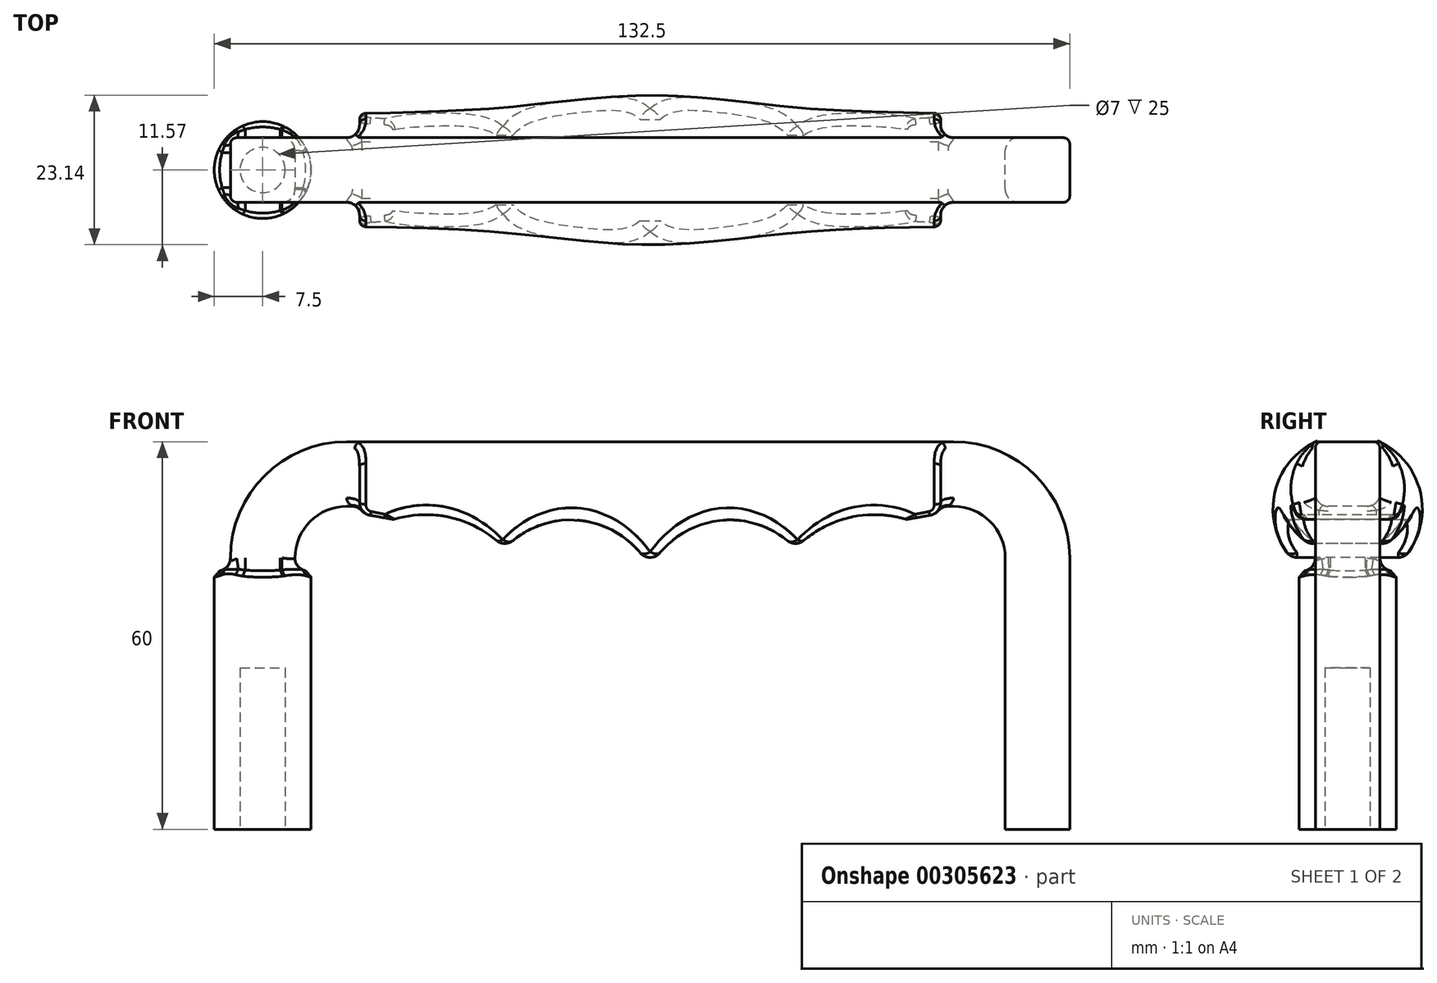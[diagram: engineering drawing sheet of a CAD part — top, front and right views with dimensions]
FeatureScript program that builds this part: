
annotation { "Feature Type Name" : "Feature", "Feature Type Description" : "" }
export const myFeature = defineFeature(function(context is Context, id is Id, definition is map)
    precondition{}
    {
        {
            var Q0;
            Q0=qCreatedBy(makeId("Front.planeOp"),FACE);
            var sketch = newSketch(context, id + "F0", { "sketchPlane" : qUnion([Q0])});
            skLineSegment(sketch, "E0", {"start": v(-60, 0) * mm, "end": v(-60, 55) * mm});
            skLineSegment(sketch, "E1", {"start": v(-60, 55) * mm, "end": v(60, 55) * mm});
            skLineSegment(sketch, "E2", {"start": v(60, 55) * mm, "end": v(60, 0) * mm});
            skPoint(sketch, "E3", {"position": v(0, 55) * mm});
            skSolve(sketch);
        }
        {
            var Q0;
            Q0=sQuery(id+"F0.wireOp",EDGE,"E0");
            var Q1;
            Q1=sQuery(id+"F0.wireOp",VERTEX,"E0.start");
            cPlane(context, id + "F1", {"entities" : qUnion([Q0, Q1]), "cplaneType" : CPlaneType.CURVE_POINT, "offset" : 25 * mm, "width" : 150 * mm, "height" : 150 * mm});
        }
        {
            var Q0;
            Q0=qCreatedBy(id+"F1.planeOp",FACE);
            var sketch = newSketch(context, id + "F2", { "sketchPlane" : qUnion([Q0])});
            skLineSegment(sketch, "E4.bottom", {"start": v(-55, -5) * mm, "end": v(-65, -5) * mm});
            skLineSegment(sketch, "E4.top", {"start": v(-55, 5) * mm, "end": v(-65, 5) * mm});
            skLineSegment(sketch, "E4.left", {"start": v(-55, -5) * mm, "end": v(-55, 5) * mm});
            skLineSegment(sketch, "E4.right", {"start": v(-65, -5) * mm, "end": v(-65, 5) * mm});
            skPoint(sketch, "E4.middle", {"position": v(-60, 0) * mm});
            skSolve(sketch);
        }
        {
            var Q0;
            Q0=makeQuery(id+"F2.imprint","IMPRINT",FACE,{"disambiguationData":[TD([[makeQuery(id+"F2.imprint","IMPRINT",EDGE,{"derivedFrom":sQuery(id+"F2.wireOp",EDGE,"E4.bottom")}),-1.0]])]});
            var Q1;
            Q1=sQuery(id+"F0.wireOp",EDGE,"E0");
            var Q2;
            Q2=sQuery(id+"F0.wireOp",EDGE,"E1");
            var Q3;
            Q3=sQuery(id+"F0.wireOp",EDGE,"E2");
            sweep(context, id + "F3", {"profiles" : qUnion([Q0]), "path" : qUnion([Q1, Q2, Q3])});
        }
        {
            var Q0;
            Q0=makeQuery(id+"F3.opSweep","CAP_FACE",FACE,{"disambiguationData":[OSD([sQuery(id+"F0.wireOp",VERTEX,"E0.start"),sQuery(id+"F2.wireOp",EDGE,"E4.bottom"),sQuery(id+"F2.wireOp",EDGE,"E4.top"),sQuery(id+"F2.wireOp",EDGE,"E4.left"),sQuery(id+"F2.wireOp",EDGE,"E4.right")])],"isStart":true});
            var sketch = newSketch(context, id + "F4", { "sketchPlane" : qUnion([Q0])});
            skCircle(sketch, "E5", {"center": v(-60, 0) * mm, "radius": 7.5 * mm});
            skSolve(sketch);
        }
        {
            var Q0;
            Q0 = qSketchRegion(id + "F4", true);
            extrude(context, id + "F5", {"entities" : qUnion([Q0]), "operationType" : NewBodyOperationType.ADD, "oppositeDirection" : true, "depth" : 40 * mm});
        }
        {
            var Q0;
            Q0=qCreatedBy(makeId("Front.planeOp"),FACE);
            var sketch = newSketch(context, id + "F6", { "sketchPlane" : qUnion([Q0])});
            skPoint(sketch, "E6", {"position": v(-22.5, 42) * mm});
            skPoint(sketch, "E7", {"position": v(0, 38) * mm});
            skPoint(sketch, "E8", {"position": v(45, 44) * mm});
            skPoint(sketch, "E9", {"position": v(-45, 44) * mm});
            skPoint(sketch, "E10.center.orphan", {"position": v(22.5, 42) * mm});
            skArc(sketch, "E11", {"start": v(-22.5, 42) * mm, "mid": v(-33.34, 47.65) * mm, "end": v(-45, 44) * mm});
            skArc(sketch, "E12", {"start": v(0, 38) * mm, "mid": v(-10.06, 46.7) * mm, "end": v(-22.5, 42) * mm});
            skArc(sketch, "E13", {"start": v(22.5, 42) * mm, "mid": v(10.06, 46.7) * mm, "end": v(0, 38) * mm});
            skArc(sketch, "E14", {"start": v(45, 44) * mm, "mid": v(33.34, 47.65) * mm, "end": v(22.5, 42) * mm});
            skSolve(sketch);
        }
        {
            var Q0;
            Q0=makeQuery(id+"F3.opSweep","SWEPT_FACE",FACE,{"disambiguationData":[OSD([sQuery(id+"F0.wireOp",EDGE,"E0"),sQuery(id+"F2.wireOp",EDGE,"E4.left")])]});
            var Q1;
            Q1=sQuery(id+"F6.wireOp",VERTEX,"E9");
            cPlane(context, id + "F7", {"entities" : qUnion([Q0, Q1]), "cplaneType" : CPlaneType.PLANE_POINT, "offset" : 25 * mm, "width" : 150 * mm, "height" : 150 * mm});
        }
        {
            var Q0;
            Q0=qCreatedBy(id+"F7.planeOp",FACE);
            var sketch = newSketch(context, id + "F8", { "sketchPlane" : qUnion([Q0])});
            skCircle(sketch, "E15", {"center": v(0, 52.78) * mm, "radius": 8.78 * mm});
            skPoint(sketch, "E15.first.point", {"position": v(-5, 60) * mm});
            skPoint(sketch, "E15.second.point", {"position": v(5, 60) * mm});
            skPoint(sketch, "E15.third.point", {"position": v(0, 44) * mm});
            skSolve(sketch);
        }
        {
            var Q0;
            Q0=qCreatedBy(id+"F7.planeOp",FACE);
            var Q1;
            Q1=sQuery(id+"F6.wireOp",VERTEX,"E6");
            cPlane(context, id + "F9", {"entities" : qUnion([Q0, Q1]), "cplaneType" : CPlaneType.PLANE_POINT, "offset" : 25 * mm, "width" : 150 * mm, "height" : 150 * mm});
        }
        {
            var Q0;
            Q0=qCreatedBy(id+"F9.planeOp",FACE);
            var sketch = newSketch(context, id + "F10", { "sketchPlane" : qUnion([Q0])});
            skCircle(sketch, "E16", {"center": v(0, 51.7) * mm, "radius": 9.7 * mm});
            skPoint(sketch, "E16.first.point", {"position": v(-5, 60) * mm});
            skPoint(sketch, "E16.second.point", {"position": v(5, 60) * mm});
            skPoint(sketch, "E16.third.point", {"position": v(0, 42) * mm});
            skSolve(sketch);
        }
        {
            var Q0;
            Q0=qCreatedBy(id+"F9.planeOp",FACE);
            var Q1;
            Q1=sQuery(id+"F6.wireOp",VERTEX,"E7");
            cPlane(context, id + "F11", {"entities" : qUnion([Q0, Q1]), "cplaneType" : CPlaneType.PLANE_POINT, "offset" : 25 * mm, "width" : 150 * mm, "height" : 150 * mm});
        }
        {
            var Q0;
            Q0=qCreatedBy(id+"F11.planeOp",FACE);
            var sketch = newSketch(context, id + "F12", { "sketchPlane" : qUnion([Q0])});
            skCircle(sketch, "E17", {"center": v(0, 49.57) * mm, "radius": 11.57 * mm});
            skPoint(sketch, "E17.first.point", {"position": v(-5, 60) * mm});
            skPoint(sketch, "E17.second.point", {"position": v(5, 60) * mm});
            skPoint(sketch, "E17.third.point", {"position": v(0, 38) * mm});
            skSolve(sketch);
        }
        {
            var Q0;
            Q0=qCreatedBy(id+"F11.planeOp",FACE);
            var Q1;
            Q1=sQuery(id+"F6.wireOp",VERTEX,"E10.center.orphan");
            cPlane(context, id + "F13", {"entities" : qUnion([Q0, Q1]), "cplaneType" : CPlaneType.PLANE_POINT, "offset" : 25 * mm, "width" : 150 * mm, "height" : 150 * mm});
        }
        {
            var Q0;
            Q0=qCreatedBy(id+"F13.planeOp",FACE);
            var sketch = newSketch(context, id + "F14", { "sketchPlane" : qUnion([Q0])});
            skCircle(sketch, "E18", {"center": v(0, 51.7) * mm, "radius": 9.7 * mm});
            skPoint(sketch, "E18.first.point", {"position": v(-5, 60) * mm});
            skPoint(sketch, "E18.second.point", {"position": v(5, 60) * mm});
            skPoint(sketch, "E18.third.point", {"position": v(0, 42) * mm});
            skSolve(sketch);
        }
        {
            var Q0;
            Q0=qCreatedBy(id+"F13.planeOp",FACE);
            var Q1;
            Q1=sQuery(id+"F6.wireOp",VERTEX,"E8");
            cPlane(context, id + "F15", {"entities" : qUnion([Q0, Q1]), "cplaneType" : CPlaneType.PLANE_POINT, "offset" : 25 * mm, "width" : 150 * mm, "height" : 150 * mm});
        }
        {
            var Q0;
            Q0=qCreatedBy(id+"F15.planeOp",FACE);
            var sketch = newSketch(context, id + "F16", { "sketchPlane" : qUnion([Q0])});
            skCircle(sketch, "E19", {"center": v(0, 52.78) * mm, "radius": 8.78 * mm});
            skPoint(sketch, "E19.first.point", {"position": v(-5, 60) * mm});
            skPoint(sketch, "E19.second.point", {"position": v(5, 60) * mm});
            skPoint(sketch, "E19.third.point", {"position": v(0, 44) * mm});
            skSolve(sketch);
        }
        {
            var Q1;
            Q1=makeQuery(id+"F8.imprint","IMPRINT",FACE,{"disambiguationData":[TD([[makeQuery(id+"F8.imprint","IMPRINT",EDGE,{"derivedFrom":sQuery(id+"F8.wireOp",EDGE,"E15")}),1.0]])]});
            var Q2;
            Q2=makeQuery(id+"F10.imprint","IMPRINT",FACE,{"disambiguationData":[TD([[makeQuery(id+"F10.imprint","IMPRINT",EDGE,{"derivedFrom":sQuery(id+"F10.wireOp",EDGE,"E16")}),1.0]])]});
            var Q3;
            Q3=makeQuery(id+"F12.imprint","IMPRINT",FACE,{"disambiguationData":[TD([[makeQuery(id+"F12.imprint","IMPRINT",EDGE,{"derivedFrom":sQuery(id+"F12.wireOp",EDGE,"E17")}),1.0]])]});
            var Q4;
            Q4=makeQuery(id+"F14.imprint","IMPRINT",FACE,{"disambiguationData":[TD([[makeQuery(id+"F14.imprint","IMPRINT",EDGE,{"derivedFrom":sQuery(id+"F14.wireOp",EDGE,"E18")}),1.0]])]});
            var Q5;
            Q5=makeQuery(id+"F16.imprint","IMPRINT",FACE,{"disambiguationData":[TD([[makeQuery(id+"F16.imprint","IMPRINT",EDGE,{"derivedFrom":sQuery(id+"F16.wireOp",EDGE,"E19")}),1.0]])]});
            var Q6;
            Q6=sQuery(id+"F6.wireOp",EDGE,"E11");
            var Q7;
            Q7=sQuery(id+"F6.wireOp",EDGE,"E12");
            var Q8;
            Q8=sQuery(id+"F6.wireOp",EDGE,"E13");
            var Q9;
            Q9=sQuery(id+"F6.wireOp",EDGE,"E14");
            loft(context, id + "F17", {"sheetProfilesArray" : [{ "sheetProfileEntities" : qUnion([Q1]) }, { "sheetProfileEntities" : qUnion([Q2]) }, { "sheetProfileEntities" : qUnion([Q3]) }, { "sheetProfileEntities" : qUnion([Q4]) }, { "sheetProfileEntities" : qUnion([Q5]) }], "guidesArray" : [{ "guideEntities" : qUnion([Q6]), "guideDerivativeType" : LoftGuideDerivativeType.DEFAULT, "guideDerivativeMagnitude" : 1 }, { "guideEntities" : qUnion([Q7]), "guideDerivativeType" : LoftGuideDerivativeType.DEFAULT, "guideDerivativeMagnitude" : 1 }, { "guideEntities" : qUnion([Q8]), "guideDerivativeType" : LoftGuideDerivativeType.DEFAULT, "guideDerivativeMagnitude" : 1 }, { "guideEntities" : qUnion([Q9]), "guideDerivativeType" : LoftGuideDerivativeType.DEFAULT, "guideDerivativeMagnitude" : 1 }]});
        }
        {
            var Q0;
            Q0=qCreatedBy(makeId("Front.planeOp"),FACE);
            var sketch = newSketch(context, id + "F18", { "sketchPlane" : qUnion([Q0])});
            skPoint(sketch, "E20.0", {"position": v(-22.5, 42) * mm});
            skPoint(sketch, "E20.1", {"position": v(0, 38) * mm});
            skPoint(sketch, "E20.2", {"position": v(45, 44) * mm});
            skPoint(sketch, "E20.3", {"position": v(-45, 44) * mm});
            skPoint(sketch, "E20.4", {"position": v(22.5, 42) * mm});
            skArc(sketch, "E20.5", {"start": v(-22.5, 42) * mm, "mid": v(-33.34, 47.65) * mm, "end": v(-45, 44) * mm, "construction": true});
            skArc(sketch, "E20.6", {"start": v(0, 38) * mm, "mid": v(-10.06, 46.7) * mm, "end": v(-22.5, 42) * mm, "construction": true});
            skArc(sketch, "E20.7", {"start": v(22.5, 42) * mm, "mid": v(10.06, 46.7) * mm, "end": v(0, 38) * mm, "construction": true});
            skArc(sketch, "E20.8", {"start": v(45, 44) * mm, "mid": v(33.34, 47.65) * mm, "end": v(22.5, 42) * mm, "construction": true});
            skLineSegment(sketch, "E21", {"start": v(-45, 44) * mm, "end": v(-45, 13.66) * mm, "construction": true});
            skLineSegment(sketch, "E22", {"start": v(-45, 13.66) * mm, "end": v(45, 13.66) * mm, "construction": true});
            skLineSegment(sketch, "E23", {"start": v(45, 13.66) * mm, "end": v(45, 44) * mm, "construction": true});
            skArc(sketch, "E24.0", {"start": v(0, 40.52) * mm, "mid": v(-10.5, 47.77) * mm, "end": v(-22.51, 43.5) * mm});
            skArc(sketch, "E24.1", {"start": v(22.51, 43.5) * mm, "mid": v(10.5, 47.77) * mm, "end": v(0, 40.52) * mm});
            skLineSegment(sketch, "E24.2", {"start": v(-46, 44.46) * mm, "end": v(-46, 12.66) * mm});
            skLineSegment(sketch, "E24.3", {"start": v(-46, 12.66) * mm, "end": v(46, 12.66) * mm});
            skLineSegment(sketch, "E24.4", {"start": v(46, 12.66) * mm, "end": v(46, 44.46) * mm});
            skArc(sketch, "E24.5", {"start": v(-22.51, 43.5) * mm, "mid": v(-34.07, 48.7) * mm, "end": v(-46, 44.46) * mm});
            skArc(sketch, "E24.6", {"start": v(46, 44.46) * mm, "mid": v(34.07, 48.7) * mm, "end": v(22.51, 43.5) * mm});
            skSolve(sketch);
        }
        {
            var Q0;
            Q0 = qSketchRegion(id + "F18", true);
            extrude(context, id + "F19", {"entities" : qUnion([Q0]), "operationType" : NewBodyOperationType.REMOVE, "endBound" : BoundingType.SYMMETRIC, "oppositeDirection" : true, "depth" : 25 * mm});
        }
        {
            var Q0;
            Q0=makeQuery(id+"F19.boolean.opBoolean","COPY",EDGE,{"derivedFrom":makeQuery(id+"F19.opExtrude","SWEPT_EDGE",EDGE,{"disambiguationData":[OSD([sQuery(id+"F18.wireOp",EDGE,"E24.0"),sQuery(id+"F18.wireOp",EDGE,"E24.5")])]})});
            var Q1;
            Q1=makeQuery(id+"F19.boolean.opBoolean","COPY",EDGE,{"derivedFrom":makeQuery(id+"F19.opExtrude","SWEPT_EDGE",EDGE,{"disambiguationData":[OSD([sQuery(id+"F18.wireOp",EDGE,"E24.0"),sQuery(id+"F18.wireOp",EDGE,"E24.1")])]})});
            var Q2;
            Q2=makeQuery(id+"F19.boolean.opBoolean","COPY",EDGE,{"derivedFrom":makeQuery(id+"F19.opExtrude","SWEPT_EDGE",EDGE,{"disambiguationData":[OSD([sQuery(id+"F18.wireOp",EDGE,"E24.1"),sQuery(id+"F18.wireOp",EDGE,"E24.6")])]})});
            fillet(context, id + "F20", {"entities" : qUnion([Q0, Q1, Q2]), "radius" : 2 * mm, "tangentPropagation" : true, "allowEdgeOverflow" : false});
        }
        {
            var Q0;
            Q0=makeQuery(id+"F19.boolean.opBoolean","INTERSECT",EDGE,{"disambiguationData":[OD(0.0)],"derivedFrom":[makeQuery(id+"F17.opLoft","SWEPT_FACE",FACE,{"disambiguationData":[OSD([sQuery(id+"F8.wireOp",EDGE,"E15"),sQuery(id+"F10.wireOp",EDGE,"E16")])]}),makeQuery(id+"F19.opExtrude","SWEPT_FACE",FACE,{"disambiguationData":[OSD([sQuery(id+"F18.wireOp",EDGE,"E24.5")])]})]});
            var Q1;
            Q1=makeQuery(id+"F19.boolean.opBoolean","INTERSECT",EDGE,{"disambiguationData":[OD(0.0)],"derivedFrom":[makeQuery(id+"F17.opLoft","SWEPT_FACE",FACE,{"disambiguationData":[OSD([sQuery(id+"F8.wireOp",EDGE,"E15"),sQuery(id+"F10.wireOp",EDGE,"E16")])]}),makeQuery(id+"F19.opExtrude","SWEPT_FACE",FACE,{"disambiguationData":[OSD([sQuery(id+"F18.wireOp",EDGE,"E24.0")])]})]});
            var Q2;
            Q2=makeQuery(id+"F19.boolean.opBoolean","INTERSECT",EDGE,{"disambiguationData":[OD(0.0)],"derivedFrom":[makeQuery(id+"F17.opLoft","SWEPT_FACE",FACE,{"disambiguationData":[OSD([sQuery(id+"F8.wireOp",EDGE,"E15"),sQuery(id+"F10.wireOp",EDGE,"E16")])]}),makeQuery(id+"F19.opExtrude","SWEPT_FACE",FACE,{"disambiguationData":[OSD([sQuery(id+"F18.wireOp",EDGE,"E24.1")])]})]});
            var Q3;
            Q3=makeQuery(id+"F19.boolean.opBoolean","INTERSECT",EDGE,{"disambiguationData":[OD(0.0)],"derivedFrom":[makeQuery(id+"F17.opLoft","SWEPT_FACE",FACE,{"disambiguationData":[OSD([sQuery(id+"F8.wireOp",EDGE,"E15"),sQuery(id+"F10.wireOp",EDGE,"E16")])]}),makeQuery(id+"F19.opExtrude","SWEPT_FACE",FACE,{"disambiguationData":[OSD([sQuery(id+"F18.wireOp",EDGE,"E24.6")])]})]});
            var Q4;
            Q4=makeQuery(id+"F19.boolean.opBoolean","INTERSECT",EDGE,{"disambiguationData":[OD(1.0)],"derivedFrom":[makeQuery(id+"F17.opLoft","SWEPT_FACE",FACE,{"disambiguationData":[OSD([sQuery(id+"F8.wireOp",EDGE,"E15"),sQuery(id+"F10.wireOp",EDGE,"E16")])]}),makeQuery(id+"F19.opExtrude","SWEPT_FACE",FACE,{"disambiguationData":[OSD([sQuery(id+"F18.wireOp",EDGE,"E24.6")])]})]});
            var Q5;
            Q5=makeQuery(id+"F19.boolean.opBoolean","INTERSECT",EDGE,{"disambiguationData":[OD(1.0)],"derivedFrom":[makeQuery(id+"F17.opLoft","SWEPT_FACE",FACE,{"disambiguationData":[OSD([sQuery(id+"F8.wireOp",EDGE,"E15"),sQuery(id+"F10.wireOp",EDGE,"E16")])]}),makeQuery(id+"F19.opExtrude","SWEPT_FACE",FACE,{"disambiguationData":[OSD([sQuery(id+"F18.wireOp",EDGE,"E24.1")])]})]});
            var Q6;
            Q6=makeQuery(id+"F19.boolean.opBoolean","INTERSECT",EDGE,{"disambiguationData":[OD(1.0)],"derivedFrom":[makeQuery(id+"F17.opLoft","SWEPT_FACE",FACE,{"disambiguationData":[OSD([sQuery(id+"F8.wireOp",EDGE,"E15"),sQuery(id+"F10.wireOp",EDGE,"E16")])]}),makeQuery(id+"F19.opExtrude","SWEPT_FACE",FACE,{"disambiguationData":[OSD([sQuery(id+"F18.wireOp",EDGE,"E24.0")])]})]});
            var Q7;
            Q7=makeQuery(id+"F19.boolean.opBoolean","INTERSECT",EDGE,{"disambiguationData":[OD(1.0)],"derivedFrom":[makeQuery(id+"F17.opLoft","SWEPT_FACE",FACE,{"disambiguationData":[OSD([sQuery(id+"F8.wireOp",EDGE,"E15"),sQuery(id+"F10.wireOp",EDGE,"E16")])]}),makeQuery(id+"F19.opExtrude","SWEPT_FACE",FACE,{"disambiguationData":[OSD([sQuery(id+"F18.wireOp",EDGE,"E24.5")])]})]});
            fillet(context, id + "F21", {"entities" : qUnion([Q0, Q1, Q2, Q3, Q4, Q5, Q6, Q7]), "radius" : 2 * mm, "allowEdgeOverflow" : false});
        }
        {
            var Q0;
            Q0=makeQuery(id+"F3.opSweep","MID_CAP_EDGE",EDGE,{"disambiguationData":[OSD([sQuery(id+"F0.wireOp",VERTEX,"E1.start"),sQuery(id+"F2.wireOp",EDGE,"E4.left")])],"capPos":1.0});
            var Q1;
            Q1=makeQuery(id+"F3.opSweep","MID_CAP_EDGE",EDGE,{"disambiguationData":[OSD([sQuery(id+"F0.wireOp",VERTEX,"E2.start"),sQuery(id+"F2.wireOp",EDGE,"E4.left")])],"capPos":2.0});
            fillet(context, id + "F22", {"entities" : qUnion([Q0, Q1]), "radius" : 8 * mm, "tangentPropagation" : true, "allowEdgeOverflow" : false});
        }
        {
            var Q0;
            Q0=makeQuery(id+"F3.opSweep","MID_CAP_EDGE",EDGE,{"disambiguationData":[OSD([sQuery(id+"F0.wireOp",VERTEX,"E1.start"),sQuery(id+"F2.wireOp",EDGE,"E4.right")])],"capPos":1.0});
            var Q1;
            Q1=makeQuery(id+"F3.opSweep","MID_CAP_EDGE",EDGE,{"disambiguationData":[OSD([sQuery(id+"F0.wireOp",VERTEX,"E2.start"),sQuery(id+"F2.wireOp",EDGE,"E4.right")])],"capPos":2.0});
            fillet(context, id + "F23", {"entities" : qUnion([Q0, Q1]), "radius" : 18 * mm, "tangentPropagation" : true, "allowEdgeOverflow" : false});
        }
        {
            var Q0;
            Q0=makeQuery(id+"F3.opSweep","SWEPT_FACE",FACE,{"disambiguationData":[OSD([sQuery(id+"F0.wireOp",EDGE,"E1"),sQuery(id+"F2.wireOp",EDGE,"E4.right")])]});
            var sketch = newSketch(context, id + "F24", { "sketchPlane" : qUnion([Q0])});
            skLineSegment(sketch, "E25.bottom", {"start": v(50.27, -17.56) * mm, "end": v(-50.27, -17.56) * mm});
            skLineSegment(sketch, "E25.top", {"start": v(50.27, 17.56) * mm, "end": v(-50.27, 17.56) * mm});
            skLineSegment(sketch, "E25.left", {"start": v(50.27, -17.56) * mm, "end": v(50.27, 17.56) * mm});
            skLineSegment(sketch, "E25.right", {"start": v(-50.27, -17.56) * mm, "end": v(-50.27, 17.56) * mm});
            skPoint(sketch, "E25.middle", {"position": v(0, 0) * mm});
            skSolve(sketch);
        }
        {
            var Q0;
            Q0 = qSketchRegion(id + "F24", true);
            extrude(context, id + "F25", {"entities" : qUnion([Q0]), "operationType" : NewBodyOperationType.REMOVE, "depth" : 25 * mm});
        }
        {
            var Q0;
            Q0=makeQuery(id+"F17.opLoft","SWEPT_BODY",BODY,{"disambiguationData":[OSD([makeQuery(id+"F8.imprint","IMPRINT",FACE,{"disambiguationData":[TD([[makeQuery(id+"F8.imprint","IMPRINT",EDGE,{"derivedFrom":sQuery(id+"F8.wireOp",EDGE,"E15")}),1.0]])]}),sQuery(id+"F10.wireOp",EDGE,"E16"),sQuery(id+"F12.wireOp",EDGE,"E17"),sQuery(id+"F14.wireOp",EDGE,"E18"),makeQuery(id+"F16.imprint","IMPRINT",FACE,{"disambiguationData":[TD([[makeQuery(id+"F16.imprint","IMPRINT",EDGE,{"derivedFrom":sQuery(id+"F16.wireOp",EDGE,"E19")}),1.0]])]})])]});
            var Q1;
            Q1=makeQuery(id+"F3.opSweep","SWEPT_BODY",BODY,{"disambiguationData":[OSD([sQuery(id+"F0.wireOp",EDGE,"E2"),sQuery(id+"F2.wireOp",EDGE,"E4.bottom"),sQuery(id+"F2.wireOp",EDGE,"E4.top"),sQuery(id+"F2.wireOp",EDGE,"E4.left"),sQuery(id+"F2.wireOp",EDGE,"E4.right")])]});
            booleanBodies(context, id + "F26", {"operationType" : BooleanOperationType.UNION, "tools" : qUnion([Q0, Q1])});
        }
        {
            var Q0;
            Q0=makeQuery(id+"F22.opFillet","BLEND_EDGE",EDGE,{"blendedFrom":[makeQuery(id+"F3.opSweep","MID_CAP_EDGE",EDGE,{"disambiguationData":[OSD([sQuery(id+"F0.wireOp",VERTEX,"E1.start"),sQuery(id+"F2.wireOp",EDGE,"E4.left")])],"capPos":1.0}),makeQuery(id+"F3.opSweep","SWEPT_FACE",FACE,{"disambiguationData":[OSD([sQuery(id+"F0.wireOp",EDGE,"E0"),sQuery(id+"F2.wireOp",EDGE,"E4.bottom")])]})],"blendedInto":[makeQuery(id+"F3.opSweep","SWEPT_FACE",FACE,{"disambiguationData":[OSD([sQuery(id+"F0.wireOp",EDGE,"E0"),sQuery(id+"F2.wireOp",EDGE,"E4.bottom")])]})]});
            var Q1;
            Q1=makeQuery(id+"F22.opFillet","BLEND_EDGE",EDGE,{"blendedFrom":[makeQuery(id+"F3.opSweep","MID_CAP_EDGE",EDGE,{"disambiguationData":[OSD([sQuery(id+"F0.wireOp",VERTEX,"E1.start"),sQuery(id+"F2.wireOp",EDGE,"E4.left")])],"capPos":1.0}),makeQuery(id+"F3.opSweep","SWEPT_FACE",FACE,{"disambiguationData":[OSD([sQuery(id+"F0.wireOp",EDGE,"E0"),sQuery(id+"F2.wireOp",EDGE,"E4.top")])]})],"blendedInto":[makeQuery(id+"F3.opSweep","SWEPT_FACE",FACE,{"disambiguationData":[OSD([sQuery(id+"F0.wireOp",EDGE,"E0"),sQuery(id+"F2.wireOp",EDGE,"E4.top")])]})]});
            var Q2;
            Q2=makeQuery(id+"F22.opFillet","BLEND_EDGE",EDGE,{"blendedFrom":[makeQuery(id+"F3.opSweep","MID_CAP_EDGE",EDGE,{"disambiguationData":[OSD([sQuery(id+"F0.wireOp",VERTEX,"E2.start"),sQuery(id+"F2.wireOp",EDGE,"E4.left")])],"capPos":2.0}),makeQuery(id+"F3.opSweep","SWEPT_FACE",FACE,{"disambiguationData":[OSD([sQuery(id+"F0.wireOp",EDGE,"E0"),sQuery(id+"F2.wireOp",EDGE,"E4.bottom")])]})],"blendedInto":[makeQuery(id+"F3.opSweep","SWEPT_FACE",FACE,{"disambiguationData":[OSD([sQuery(id+"F0.wireOp",EDGE,"E0"),sQuery(id+"F2.wireOp",EDGE,"E4.bottom")])]})]});
            var Q3;
            Q3=makeQuery(id+"F22.opFillet","BLEND_EDGE",EDGE,{"blendedFrom":[makeQuery(id+"F3.opSweep","MID_CAP_EDGE",EDGE,{"disambiguationData":[OSD([sQuery(id+"F0.wireOp",VERTEX,"E2.start"),sQuery(id+"F2.wireOp",EDGE,"E4.left")])],"capPos":2.0}),makeQuery(id+"F3.opSweep","SWEPT_FACE",FACE,{"disambiguationData":[OSD([sQuery(id+"F0.wireOp",EDGE,"E0"),sQuery(id+"F2.wireOp",EDGE,"E4.top")])]})],"blendedInto":[makeQuery(id+"F3.opSweep","SWEPT_FACE",FACE,{"disambiguationData":[OSD([sQuery(id+"F0.wireOp",EDGE,"E0"),sQuery(id+"F2.wireOp",EDGE,"E4.top")])]})]});
            var Q4;
            {var subQ0=sQuery(id+"F2.wireOp",EDGE,"E4.top");var subQ1=sQuery(id+"F2.wireOp",EDGE,"E4.left");var subQ2=sQuery(id+"F0.wireOp",EDGE,"E1");Q4=makeQuery(id+"F26.opBoolean","SPLIT",EDGE,{"disambiguationData":[TD([makeQuery(id+"F17.opLoft","CAP_FACE",FACE,{"disambiguationData":[OSD([makeQuery(id+"F8.imprint","IMPRINT",FACE,{"disambiguationData":[TD([[makeQuery(id+"F8.imprint","IMPRINT",EDGE,{"derivedFrom":sQuery(id+"F8.wireOp",EDGE,"E15")}),1.0]])]})])],"isStart":true})])],"derivedFrom":makeQuery(id+"F3.opSweep","SWEPT_EDGE",EDGE,{"disambiguationData":[OSD([subQ2,subQ0,subQ1])]})});}
            var Q5;
            {var subQ0=sQuery(id+"F2.wireOp",EDGE,"E4.bottom");var subQ1=sQuery(id+"F2.wireOp",EDGE,"E4.left");var subQ2=sQuery(id+"F0.wireOp",EDGE,"E1");Q5=makeQuery(id+"F26.opBoolean","SPLIT",EDGE,{"disambiguationData":[TD([makeQuery(id+"F17.opLoft","CAP_FACE",FACE,{"disambiguationData":[OSD([makeQuery(id+"F8.imprint","IMPRINT",FACE,{"disambiguationData":[TD([[makeQuery(id+"F8.imprint","IMPRINT",EDGE,{"derivedFrom":sQuery(id+"F8.wireOp",EDGE,"E15")}),1.0]])]})])],"isStart":true})])],"derivedFrom":makeQuery(id+"F3.opSweep","SWEPT_EDGE",EDGE,{"disambiguationData":[OSD([subQ2,subQ0,subQ1])]})});}
            var Q6;
            Q6=makeQuery(id+"F3.opSweep","SWEPT_EDGE",EDGE,{"disambiguationData":[OSD([sQuery(id+"F0.wireOp",EDGE,"E0"),sQuery(id+"F2.wireOp",EDGE,"E4.top"),sQuery(id+"F2.wireOp",EDGE,"E4.left")])]});
            var Q7;
            Q7=makeQuery(id+"F3.opSweep","SWEPT_EDGE",EDGE,{"disambiguationData":[OSD([sQuery(id+"F0.wireOp",EDGE,"E0"),sQuery(id+"F2.wireOp",EDGE,"E4.bottom"),sQuery(id+"F2.wireOp",EDGE,"E4.left")])]});
            var Q8;
            {var subQ0=sQuery(id+"F2.wireOp",EDGE,"E4.top");var subQ1=sQuery(id+"F2.wireOp",EDGE,"E4.left");var subQ2=sQuery(id+"F0.wireOp",EDGE,"E1");Q8=makeQuery(id+"F26.opBoolean","SPLIT",EDGE,{"disambiguationData":[TD([makeQuery(id+"F17.opLoft","CAP_FACE",FACE,{"disambiguationData":[OSD([makeQuery(id+"F16.imprint","IMPRINT",FACE,{"disambiguationData":[TD([[makeQuery(id+"F16.imprint","IMPRINT",EDGE,{"derivedFrom":sQuery(id+"F16.wireOp",EDGE,"E19")}),1.0]])]})])],"isStart":true})])],"derivedFrom":makeQuery(id+"F3.opSweep","SWEPT_EDGE",EDGE,{"disambiguationData":[OSD([subQ2,subQ0,subQ1])]})});}
            var Q9;
            Q9=makeQuery(id+"F3.opSweep","SWEPT_EDGE",EDGE,{"disambiguationData":[OSD([sQuery(id+"F0.wireOp",EDGE,"E2"),sQuery(id+"F2.wireOp",EDGE,"E4.top"),sQuery(id+"F2.wireOp",EDGE,"E4.left")])]});
            var Q10;
            Q10=makeQuery(id+"F3.opSweep","SWEPT_EDGE",EDGE,{"disambiguationData":[OSD([sQuery(id+"F0.wireOp",EDGE,"E2"),sQuery(id+"F2.wireOp",EDGE,"E4.bottom"),sQuery(id+"F2.wireOp",EDGE,"E4.left")])]});
            var Q11;
            {var subQ0=sQuery(id+"F2.wireOp",EDGE,"E4.bottom");var subQ1=sQuery(id+"F2.wireOp",EDGE,"E4.left");var subQ2=sQuery(id+"F0.wireOp",EDGE,"E1");Q11=makeQuery(id+"F26.opBoolean","SPLIT",EDGE,{"disambiguationData":[TD([makeQuery(id+"F17.opLoft","CAP_FACE",FACE,{"disambiguationData":[OSD([makeQuery(id+"F16.imprint","IMPRINT",FACE,{"disambiguationData":[TD([[makeQuery(id+"F16.imprint","IMPRINT",EDGE,{"derivedFrom":sQuery(id+"F16.wireOp",EDGE,"E19")}),1.0]])]})])],"isStart":true})])],"derivedFrom":makeQuery(id+"F3.opSweep","SWEPT_EDGE",EDGE,{"disambiguationData":[OSD([subQ2,subQ0,subQ1])]})});}
            fillet(context, id + "F27", {"entities" : qUnion([Q0, Q1, Q2, Q3, Q4, Q5, Q6, Q7, Q8, Q9, Q10, Q11]), "radius" : 2 * mm, "tangentPropagation" : true, "allowEdgeOverflow" : false});
        }
        {
            var Q0;
            Q0=makeQuery(id+"F19.boolean.opBoolean","INTERSECT",EDGE,{"derivedFrom":[makeQuery(id+"F17.opLoft","CAP_FACE",FACE,{"disambiguationData":[OSD([makeQuery(id+"F16.imprint","IMPRINT",FACE,{"disambiguationData":[TD([[makeQuery(id+"F16.imprint","IMPRINT",EDGE,{"derivedFrom":sQuery(id+"F16.wireOp",EDGE,"E19")}),1.0]])]})])],"isStart":true}),makeQuery(id+"F19.opExtrude","SWEPT_FACE",FACE,{"disambiguationData":[OSD([sQuery(id+"F18.wireOp",EDGE,"E24.6")])]})]});
            chamfer(context, id + "F28", {"entities" : qUnion([Q0]), "chamferType" : ChamferType.OFFSET_ANGLE, "width" : 7 * mm, "oppositeDirection" : false, "angle" : 45 * degree});
        }
        {
            var Q0;
            Q0=makeQuery(id+"F19.boolean.opBoolean","INTERSECT",EDGE,{"derivedFrom":[makeQuery(id+"F17.opLoft","CAP_FACE",FACE,{"disambiguationData":[OSD([makeQuery(id+"F8.imprint","IMPRINT",FACE,{"disambiguationData":[TD([[makeQuery(id+"F8.imprint","IMPRINT",EDGE,{"derivedFrom":sQuery(id+"F8.wireOp",EDGE,"E15")}),1.0]])]})])],"isStart":true}),makeQuery(id+"F19.opExtrude","SWEPT_FACE",FACE,{"disambiguationData":[OSD([sQuery(id+"F18.wireOp",EDGE,"E24.5")])]})]});
            chamfer(context, id + "F29", {"entities" : qUnion([Q0]), "chamferType" : ChamferType.OFFSET_ANGLE, "width" : 7 * mm, "oppositeDirection" : true, "angle" : 45 * degree});
        }
        {
            var Q0;
            {var subQ0=makeQuery(id+"F17.opLoft","CAP_FACE",FACE,{"disambiguationData":[OSD([makeQuery(id+"F16.imprint","IMPRINT",FACE,{"disambiguationData":[TD([[makeQuery(id+"F16.imprint","IMPRINT",EDGE,{"derivedFrom":sQuery(id+"F16.wireOp",EDGE,"E19")}),1.0]])]})])],"isStart":true});Q0=makeQuery(id+"F28.opChamfer","BLEND_EDGE",EDGE,{"blendedFrom":[makeQuery(id+"F19.boolean.opBoolean","INTERSECT",EDGE,{"derivedFrom":[subQ0,makeQuery(id+"F19.opExtrude","SWEPT_FACE",FACE,{"disambiguationData":[OSD([sQuery(id+"F18.wireOp",EDGE,"E24.6")])]})]}),subQ0],"blendedInto":[subQ0]});}
            var Q1;
            {var subQ0=makeQuery(id+"F17.opLoft","CAP_FACE",FACE,{"disambiguationData":[OSD([makeQuery(id+"F8.imprint","IMPRINT",FACE,{"disambiguationData":[TD([[makeQuery(id+"F8.imprint","IMPRINT",EDGE,{"derivedFrom":sQuery(id+"F8.wireOp",EDGE,"E15")}),1.0]])]})])],"isStart":true});Q1=makeQuery(id+"F29.opChamfer","BLEND_EDGE",EDGE,{"blendedFrom":[makeQuery(id+"F19.boolean.opBoolean","INTERSECT",EDGE,{"derivedFrom":[subQ0,makeQuery(id+"F19.opExtrude","SWEPT_FACE",FACE,{"disambiguationData":[OSD([sQuery(id+"F18.wireOp",EDGE,"E24.5")])]})]}),subQ0],"blendedInto":[subQ0]});}
            fillet(context, id + "F30", {"entities" : qUnion([Q0, Q1]), "radius" : 2 * mm, "tangentPropagation" : true, "allowEdgeOverflow" : false});
        }
        {
            var Q0;
            Q0=makeQuery(id+"F26.opBoolean","INTERSECT",EDGE,{"derivedFrom":[makeQuery(id+"F3.opSweep","SWEPT_FACE",FACE,{"disambiguationData":[OSD([sQuery(id+"F0.wireOp",EDGE,"E0"),sQuery(id+"F2.wireOp",EDGE,"E4.bottom")])]}),makeQuery(id+"F17.opLoft","CAP_FACE",FACE,{"disambiguationData":[OSD([makeQuery(id+"F8.imprint","IMPRINT",FACE,{"disambiguationData":[TD([[makeQuery(id+"F8.imprint","IMPRINT",EDGE,{"derivedFrom":sQuery(id+"F8.wireOp",EDGE,"E15")}),1.0]])]})])],"isStart":true})]});
            var Q1;
            Q1=makeQuery(id+"F26.opBoolean","INTERSECT",EDGE,{"derivedFrom":[makeQuery(id+"F3.opSweep","SWEPT_FACE",FACE,{"disambiguationData":[OSD([sQuery(id+"F0.wireOp",EDGE,"E0"),sQuery(id+"F2.wireOp",EDGE,"E4.bottom")])]}),makeQuery(id+"F17.opLoft","CAP_FACE",FACE,{"disambiguationData":[OSD([makeQuery(id+"F16.imprint","IMPRINT",FACE,{"disambiguationData":[TD([[makeQuery(id+"F16.imprint","IMPRINT",EDGE,{"derivedFrom":sQuery(id+"F16.wireOp",EDGE,"E19")}),1.0]])]})])],"isStart":true})]});
            fillet(context, id + "F31", {"entities" : qUnion([Q0, Q1]), "radius" : 2 * mm, "tangentPropagation" : true, "allowEdgeOverflow" : false});
        }
        {
            var Q0;
            {var subQ0=makeQuery(id+"F19.opExtrude","SWEPT_FACE",FACE,{"disambiguationData":[OSD([sQuery(id+"F18.wireOp",EDGE,"E24.5")])]});Q0=makeQuery(id+"F29.opChamfer","BLEND_EDGE",EDGE,{"blendedFrom":[makeQuery(id+"F19.boolean.opBoolean","INTERSECT",EDGE,{"derivedFrom":[makeQuery(id+"F17.opLoft","CAP_FACE",FACE,{"disambiguationData":[OSD([makeQuery(id+"F8.imprint","IMPRINT",FACE,{"disambiguationData":[TD([[makeQuery(id+"F8.imprint","IMPRINT",EDGE,{"derivedFrom":sQuery(id+"F8.wireOp",EDGE,"E15")}),1.0]])]})])],"isStart":true}),subQ0]}),makeQuery(id+"F19.boolean.opBoolean","COPY",FACE,{"derivedFrom":subQ0})],"blendedInto":[makeQuery(id+"F19.boolean.opBoolean","COPY",FACE,{"derivedFrom":subQ0})]});}
            var Q1;
            {var subQ0=makeQuery(id+"F19.opExtrude","SWEPT_FACE",FACE,{"disambiguationData":[OSD([sQuery(id+"F18.wireOp",EDGE,"E24.6")])]});Q1=makeQuery(id+"F28.opChamfer","BLEND_EDGE",EDGE,{"blendedFrom":[makeQuery(id+"F19.boolean.opBoolean","INTERSECT",EDGE,{"derivedFrom":[makeQuery(id+"F17.opLoft","CAP_FACE",FACE,{"disambiguationData":[OSD([makeQuery(id+"F16.imprint","IMPRINT",FACE,{"disambiguationData":[TD([[makeQuery(id+"F16.imprint","IMPRINT",EDGE,{"derivedFrom":sQuery(id+"F16.wireOp",EDGE,"E19")}),1.0]])]})])],"isStart":true}),subQ0]}),makeQuery(id+"F19.boolean.opBoolean","COPY",FACE,{"derivedFrom":subQ0})],"blendedInto":[makeQuery(id+"F19.boolean.opBoolean","COPY",FACE,{"derivedFrom":subQ0})]});}
            fillet(context, id + "F32", {"entities" : qUnion([Q0, Q1]), "radius" : 1 * mm, "tangentPropagation" : true, "allowEdgeOverflow" : false});
        }
        {
            var Q0;
            Q0=makeQuery(id+"F23.opFillet","BLEND_EDGE",EDGE,{"blendedFrom":[makeQuery(id+"F3.opSweep","MID_CAP_EDGE",EDGE,{"disambiguationData":[OSD([sQuery(id+"F0.wireOp",VERTEX,"E1.start"),sQuery(id+"F2.wireOp",EDGE,"E4.right")])],"capPos":1.0}),makeQuery(id+"F3.opSweep","SWEPT_FACE",FACE,{"disambiguationData":[OSD([sQuery(id+"F0.wireOp",EDGE,"E0"),sQuery(id+"F2.wireOp",EDGE,"E4.bottom")])]})],"blendedInto":[makeQuery(id+"F3.opSweep","SWEPT_FACE",FACE,{"disambiguationData":[OSD([sQuery(id+"F0.wireOp",EDGE,"E0"),sQuery(id+"F2.wireOp",EDGE,"E4.bottom")])]})]});
            var Q1;
            Q1=makeQuery(id+"F23.opFillet","BLEND_EDGE",EDGE,{"blendedFrom":[makeQuery(id+"F3.opSweep","MID_CAP_EDGE",EDGE,{"disambiguationData":[OSD([sQuery(id+"F0.wireOp",VERTEX,"E2.start"),sQuery(id+"F2.wireOp",EDGE,"E4.right")])],"capPos":2.0}),makeQuery(id+"F3.opSweep","SWEPT_FACE",FACE,{"disambiguationData":[OSD([sQuery(id+"F0.wireOp",EDGE,"E0"),sQuery(id+"F2.wireOp",EDGE,"E4.bottom")])]})],"blendedInto":[makeQuery(id+"F3.opSweep","SWEPT_FACE",FACE,{"disambiguationData":[OSD([sQuery(id+"F0.wireOp",EDGE,"E0"),sQuery(id+"F2.wireOp",EDGE,"E4.bottom")])]})]});
            var Q2;
            Q2=makeQuery(id+"F23.opFillet","BLEND_EDGE",EDGE,{"blendedFrom":[makeQuery(id+"F3.opSweep","MID_CAP_EDGE",EDGE,{"disambiguationData":[OSD([sQuery(id+"F0.wireOp",VERTEX,"E2.start"),sQuery(id+"F2.wireOp",EDGE,"E4.right")])],"capPos":2.0}),makeQuery(id+"F3.opSweep","SWEPT_FACE",FACE,{"disambiguationData":[OSD([sQuery(id+"F0.wireOp",EDGE,"E0"),sQuery(id+"F2.wireOp",EDGE,"E4.top")])]})],"blendedInto":[makeQuery(id+"F3.opSweep","SWEPT_FACE",FACE,{"disambiguationData":[OSD([sQuery(id+"F0.wireOp",EDGE,"E0"),sQuery(id+"F2.wireOp",EDGE,"E4.top")])]})]});
            var Q3;
            Q3=makeQuery(id+"F23.opFillet","BLEND_EDGE",EDGE,{"blendedFrom":[makeQuery(id+"F3.opSweep","MID_CAP_EDGE",EDGE,{"disambiguationData":[OSD([sQuery(id+"F0.wireOp",VERTEX,"E1.start"),sQuery(id+"F2.wireOp",EDGE,"E4.right")])],"capPos":1.0}),makeQuery(id+"F3.opSweep","SWEPT_FACE",FACE,{"disambiguationData":[OSD([sQuery(id+"F0.wireOp",EDGE,"E0"),sQuery(id+"F2.wireOp",EDGE,"E4.top")])]})],"blendedInto":[makeQuery(id+"F3.opSweep","SWEPT_FACE",FACE,{"disambiguationData":[OSD([sQuery(id+"F0.wireOp",EDGE,"E0"),sQuery(id+"F2.wireOp",EDGE,"E4.top")])]})]});
            fillet(context, id + "F33", {"entities" : qUnion([Q0, Q1, Q2, Q3]), "radius" : 1 * mm, "tangentPropagation" : true, "allowEdgeOverflow" : false});
        }
        {
            var Q0;
            Q0=makeQuery(id+"FxCmaLql5hD37hL_1.1.F5.boolean.opBoolean","INTERSECT",EDGE,{"derivedFrom":[makeQuery(id+"F3.opSweep","SWEPT_FACE",FACE,{"disambiguationData":[OSD([sQuery(id+"F0.wireOp",EDGE,"E0"),sQuery(id+"F2.wireOp",EDGE,"E4.bottom")])]}),makeQuery(id+"FxCmaLql5hD37hL_1.1.F5.opExtrude","CAP_FACE",FACE,{"disambiguationData":[OSD([sQuery(id+"F4.wireOp",EDGE,"E5")])],"isStart":false})]});
            var Q1;
            Q1=makeQuery(id+"F5.boolean.opBoolean","INTERSECT",EDGE,{"derivedFrom":[makeQuery(id+"F3.opSweep","SWEPT_FACE",FACE,{"disambiguationData":[OSD([sQuery(id+"F0.wireOp",EDGE,"E0"),sQuery(id+"F2.wireOp",EDGE,"E4.bottom")])]}),makeQuery(id+"F5.opExtrude","CAP_FACE",FACE,{"disambiguationData":[OSD([sQuery(id+"F4.wireOp",EDGE,"E5")])],"isStart":false})]});
            fillet(context, id + "F34", {"entities" : qUnion([Q0, Q1]), "radius" : 2 * mm, "tangentPropagation" : true, "allowEdgeOverflow" : false});
        }
        {
            var Q0;
            Q0=makeQuery(id+"F5.opExtrude","CAP_EDGE",EDGE,{"disambiguationData":[OSD([sQuery(id+"F4.wireOp",EDGE,"E5")])],"isStart":false});
            var Q1;
            Q1=makeQuery(id+"FxCmaLql5hD37hL_1.1.F5.opExtrude","CAP_EDGE",EDGE,{"disambiguationData":[OSD([sQuery(id+"F4.wireOp",EDGE,"E5")])],"isStart":false});
            chamfer(context, id + "F35", {"entities" : qUnion([Q0, Q1]), "chamferType" : ChamferType.OFFSET_ANGLE, "width" : 1 * mm, "oppositeDirection" : false, "angle" : 45 * degree, "tangentPropagation" : true});
        }
        {
            var Q0;
            Q0=makeQuery(id+"F5.boolean.opBoolean","MERGE",FACE,{"derivedFrom":[makeQuery(id+"F3.opSweep","CAP_FACE",FACE,{"disambiguationData":[OSD([sQuery(id+"F0.wireOp",VERTEX,"E0.start"),sQuery(id+"F2.wireOp",EDGE,"E4.bottom"),sQuery(id+"F2.wireOp",EDGE,"E4.top"),sQuery(id+"F2.wireOp",EDGE,"E4.left"),sQuery(id+"F2.wireOp",EDGE,"E4.right")])],"isStart":true}),makeQuery(id+"F5.opExtrude","CAP_FACE",FACE,{"disambiguationData":[OSD([sQuery(id+"F4.wireOp",EDGE,"E5")])],"isStart":true})]});
            var sketch = newSketch(context, id + "F36", { "sketchPlane" : qUnion([Q0])});
            skCircle(sketch, "E26", {"center": v(-60, 0) * mm, "radius": 3.5 * mm});
            skSolve(sketch);
        }
        {
            var Q0;
            Q0 = qSketchRegion(id + "F36", true);
            extrude(context, id + "F37", {"entities" : qUnion([Q0]), "operationType" : NewBodyOperationType.REMOVE, "oppositeDirection" : true, "depth" : 25 * mm});
        }
    });
